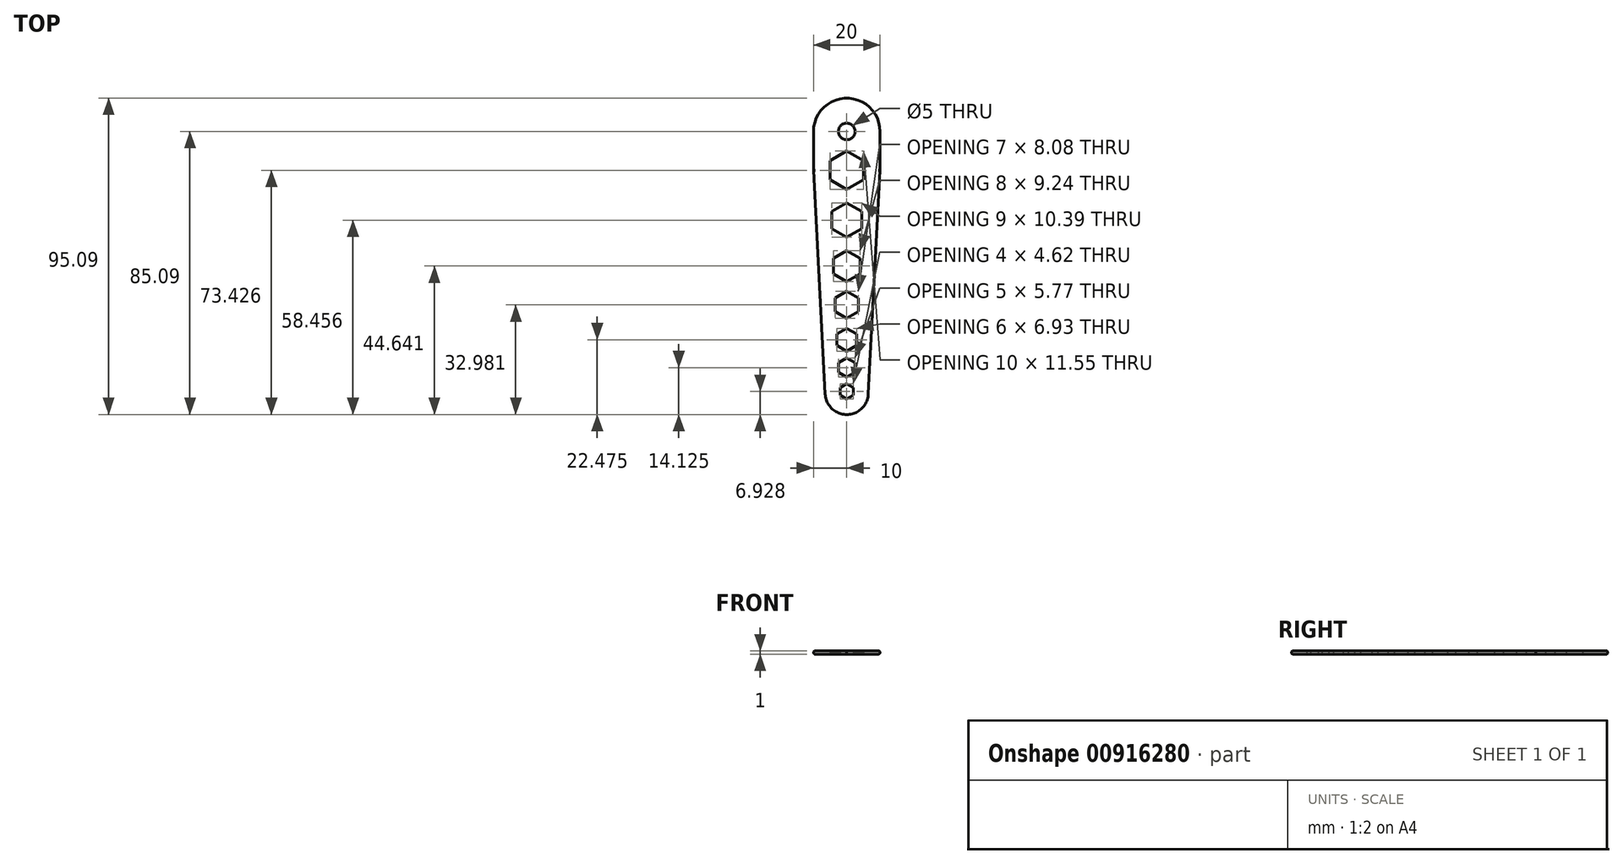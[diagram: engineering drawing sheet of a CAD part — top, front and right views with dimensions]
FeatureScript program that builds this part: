
annotation { "Feature Type Name" : "Feature", "Feature Type Description" : "" }
export const myFeature = defineFeature(function(context is Context, id is Id, definition is map)
    precondition{}
    {
        {
            var Q0;
            Q0=qCreatedBy(makeId("Top.planeOp"),FACE);
            var sketch = newSketch(context, id + "F0", { "sketchPlane" : qUnion([Q0])});
            skLineSegment(sketch, "E0.bottom", {"start": v(-10, 45) * mm, "end": v(10, 45) * mm, "construction": true});
            skLineSegment(sketch, "E0.left", {"start": v(-10, 45) * mm, "end": v(-10, -45) * mm, "construction": true});
            skLineSegment(sketch, "E0.right", {"start": v(10, 45) * mm, "end": v(10, -45) * mm, "construction": true});
            skPoint(sketch, "E0.middle", {"position": v(0, 0) * mm});
            skLineSegment(sketch, "E1", {"start": v(10, 35) * mm, "end": v(10, 23.34) * mm});
            skLineSegment(sketch, "E2", {"start": v(10, 23.34) * mm, "end": v(6.16, -50.09) * mm});
            skLineSegment(sketch, "E3", {"start": v(6.16, -50.09) * mm, "end": v(0, -50.09) * mm});
            skLineSegment(sketch, "E4", {"start": v(0, 45) * mm, "end": v(0, 45) * mm});
            skLineSegment(sketch, "E5.MirrorCS", {"start": v(-10, 23.34) * mm, "end": v(-6.16, -50.09) * mm});
            skLineSegment(sketch, "E6", {"start": v(-10, 23.34) * mm, "end": v(-10, 35) * mm});
            skLineSegment(sketch, "E7", {"start": v(-6.16, -50.09) * mm, "end": v(0, -50.09) * mm});
            skCircle(sketch, "E8", {"center": v(0, 35) * mm, "radius": 2.5 * mm});
            skPoint(sketch, "E9.visualSharp", {"position": v(-10, 45) * mm});
            skArc(sketch, "E9.filletArc", {"start": v(0, 45) * mm, "mid": v(-7.07, 42.07) * mm, "end": v(-10, 35) * mm});
            skPoint(sketch, "E10.visualSharp", {"position": v(10, 45) * mm});
            skArc(sketch, "E10.filletArc", {"start": v(10, 35) * mm, "mid": v(7.07, 42.07) * mm, "end": v(0, 45) * mm});
            skCircle(sketch, "E11.cCircle", {"center": v(0, 23.34) * mm, "radius": 5 * mm, "construction": true});
            skLineSegment(sketch, "E11.0", {"start": v(5, 26.22) * mm, "end": v(5, 20.45) * mm});
            skLineSegment(sketch, "E11.1", {"start": v(5, 20.45) * mm, "end": v(0, 17.56) * mm});
            skLineSegment(sketch, "E11.2", {"start": v(0, 17.56) * mm, "end": v(-5, 20.45) * mm});
            skLineSegment(sketch, "E11.3", {"start": v(-5, 20.45) * mm, "end": v(-5, 26.22) * mm});
            skLineSegment(sketch, "E11.4", {"start": v(-5, 26.22) * mm, "end": v(0, 29.1) * mm});
            skLineSegment(sketch, "E11.5", {"start": v(0, 29.1) * mm, "end": v(5, 26.22) * mm});
            skPoint(sketch, "E11.0.midPoint", {"position": v(5, 23.34) * mm});
            skCircle(sketch, "E12.cCircle", {"center": v(0, -27.61) * mm, "radius": 3 * mm, "construction": true});
            skLineSegment(sketch, "E12.0", {"start": v(3, -25.88) * mm, "end": v(3, -29.35) * mm});
            skLineSegment(sketch, "E12.1", {"start": v(3, -29.35) * mm, "end": v(0, -31.08) * mm});
            skLineSegment(sketch, "E12.2", {"start": v(0, -31.08) * mm, "end": v(-3, -29.35) * mm});
            skLineSegment(sketch, "E12.3", {"start": v(-3, -29.35) * mm, "end": v(-3, -25.88) * mm});
            skLineSegment(sketch, "E12.4", {"start": v(-3, -25.88) * mm, "end": v(0, -24.15) * mm});
            skLineSegment(sketch, "E12.5", {"start": v(0, -24.15) * mm, "end": v(3, -25.88) * mm});
            skPoint(sketch, "E12.0.midPoint", {"position": v(3, -27.61) * mm});
            skCircle(sketch, "E13.cCircle", {"center": v(0, -35.97) * mm, "radius": 2.5 * mm, "construction": true});
            skLineSegment(sketch, "E13.0", {"start": v(2.5, -34.52) * mm, "end": v(2.5, -37.4) * mm});
            skLineSegment(sketch, "E13.1", {"start": v(2.5, -37.4) * mm, "end": v(0, -38.85) * mm});
            skLineSegment(sketch, "E13.2", {"start": v(0, -38.85) * mm, "end": v(-2.5, -37.4) * mm});
            skLineSegment(sketch, "E13.3", {"start": v(-2.5, -37.4) * mm, "end": v(-2.5, -34.52) * mm});
            skLineSegment(sketch, "E13.4", {"start": v(-2.5, -34.52) * mm, "end": v(0, -33.08) * mm});
            skLineSegment(sketch, "E13.5", {"start": v(0, -33.08) * mm, "end": v(2.5, -34.52) * mm});
            skPoint(sketch, "E13.0.midPoint", {"position": v(2.5, -35.97) * mm});
            skCircle(sketch, "E14.cCircle", {"center": v(0, -43.16) * mm, "radius": 2 * mm, "construction": true});
            skLineSegment(sketch, "E14.0", {"start": v(2, -42) * mm, "end": v(2, -44.32) * mm});
            skLineSegment(sketch, "E14.1", {"start": v(2, -44.32) * mm, "end": v(0, -45.47) * mm});
            skLineSegment(sketch, "E14.2", {"start": v(0, -45.47) * mm, "end": v(-2, -44.32) * mm});
            skLineSegment(sketch, "E14.3", {"start": v(-2, -44.32) * mm, "end": v(-2, -42) * mm});
            skLineSegment(sketch, "E14.4", {"start": v(-2, -42) * mm, "end": v(0, -40.85) * mm});
            skLineSegment(sketch, "E14.5", {"start": v(0, -40.85) * mm, "end": v(2, -42) * mm});
            skPoint(sketch, "E14.0.midPoint", {"position": v(2, -43.16) * mm});
            skCircle(sketch, "E15.cCircle", {"center": v(0, 8.37) * mm, "radius": 4.5 * mm, "construction": true});
            skLineSegment(sketch, "E15.0", {"start": v(4.5, 10.96) * mm, "end": v(4.5, 5.77) * mm});
            skLineSegment(sketch, "E15.1", {"start": v(4.5, 5.77) * mm, "end": v(0, 3.17) * mm});
            skLineSegment(sketch, "E15.2", {"start": v(0, 3.17) * mm, "end": v(-4.5, 5.77) * mm});
            skLineSegment(sketch, "E15.3", {"start": v(-4.5, 5.77) * mm, "end": v(-4.5, 10.96) * mm});
            skLineSegment(sketch, "E15.4", {"start": v(-4.5, 10.96) * mm, "end": v(0, 13.56) * mm});
            skLineSegment(sketch, "E15.5", {"start": v(0, 13.56) * mm, "end": v(4.5, 10.96) * mm});
            skPoint(sketch, "E15.0.midPoint", {"position": v(4.5, 8.37) * mm});
            skCircle(sketch, "E16.cCircle", {"center": v(0, -5.45) * mm, "radius": 4 * mm, "construction": true});
            skLineSegment(sketch, "E16.0", {"start": v(4, -3.14) * mm, "end": v(4, -7.76) * mm});
            skLineSegment(sketch, "E16.1", {"start": v(4, -7.76) * mm, "end": v(0, -10.07) * mm});
            skLineSegment(sketch, "E16.2", {"start": v(0, -10.07) * mm, "end": v(-4, -7.76) * mm});
            skLineSegment(sketch, "E16.3", {"start": v(-4, -7.76) * mm, "end": v(-4, -3.14) * mm});
            skLineSegment(sketch, "E16.4", {"start": v(-4, -3.14) * mm, "end": v(0, -0.83) * mm});
            skLineSegment(sketch, "E16.5", {"start": v(0, -0.83) * mm, "end": v(4, -3.14) * mm});
            skPoint(sketch, "E16.0.midPoint", {"position": v(4, -5.45) * mm});
            skCircle(sketch, "E17.cCircle", {"center": v(0, -17.1) * mm, "radius": 3.5 * mm, "construction": true});
            skLineSegment(sketch, "E17.0", {"start": v(3.5, -15.09) * mm, "end": v(3.5, -19.13) * mm});
            skLineSegment(sketch, "E17.1", {"start": v(3.5, -19.13) * mm, "end": v(0, -21.15) * mm});
            skLineSegment(sketch, "E17.2", {"start": v(0, -21.15) * mm, "end": v(-3.5, -19.13) * mm});
            skLineSegment(sketch, "E17.3", {"start": v(-3.5, -19.13) * mm, "end": v(-3.5, -15.09) * mm});
            skLineSegment(sketch, "E17.4", {"start": v(-3.5, -15.09) * mm, "end": v(0, -13.07) * mm});
            skLineSegment(sketch, "E17.5", {"start": v(0, -13.07) * mm, "end": v(3.5, -15.09) * mm});
            skPoint(sketch, "E17.0.midPoint", {"position": v(3.5, -17.1) * mm});
            skSolve(sketch);
        }
        {
            var Q0;
            Q0=makeQuery(id+"F0.imprint","IMPRINT",FACE,{"disambiguationData":[TD([[makeQuery(id+"F0.imprint","IMPRINT",EDGE,{"derivedFrom":sQuery(id+"F0.wireOp",EDGE,"660UfFcq-DxuX-vggt-8gqN-h0Q4Ah5XbNWX")}),-1.0]])]});
            var Q1;
            Q1=makeQuery(id+"F0.imprint","IMPRINT",FACE,{"disambiguationData":[TD([[makeQuery(id+"F0.imprint","IMPRINT",EDGE,{"derivedFrom":sQuery(id+"F0.wireOp",EDGE,"E1")}),-1.0]])]});
            extrude(context, id + "F1", {"entities" : qUnion([Q0, Q1]), "depth" : 1 * mm, "offsetDistance" : 25 * mm});
        }
        {
            var Q0;
            Q0=makeQuery(id+"F1.opExtrude","SWEPT_EDGE",EDGE,{"disambiguationData":[OSD([sQuery(id+"F0.wireOp",EDGE,"E2"),sQuery(id+"F0.wireOp",EDGE,"E3")])]});
            var Q1;
            Q1=makeQuery(id+"F1.opExtrude","SWEPT_EDGE",EDGE,{"disambiguationData":[OSD([sQuery(id+"F0.wireOp",EDGE,"E5.MirrorCS"),sQuery(id+"F0.wireOp",EDGE,"E7")])]});
            fillet(context, id + "F2", {"entities" : qUnion([Q0, Q1]), "radius" : 6.5 * mm, "tangentPropagation" : true, "allowEdgeOverflow" : false});
        }
        {
            var Q0;
            Q0=makeQuery(id+"F1.opExtrude","CAP_EDGE",EDGE,{"disambiguationData":[OSD([sQuery(id+"F0.wireOp",EDGE,"E2")])],"isStart":false});
            var Q1;
            {var subQ0=sQuery(id+"F0.wireOp",EDGE,"E3");var subQ1=sQuery(id+"F0.wireOp",EDGE,"E2");Q1=makeQuery(id+"F2.opFillet","BLEND_EDGE",EDGE,{"blendedFrom":[makeQuery(id+"F1.opExtrude","SWEPT_EDGE",EDGE,{"disambiguationData":[OSD([subQ1,subQ0])]}),makeQuery(id+"F1.opExtrude","CAP_FACE",FACE,{"disambiguationData":[OSD([sQuery(id+"F0.wireOp",EDGE,"E1"),subQ1,subQ0,sQuery(id+"F0.wireOp",EDGE,"E5.MirrorCS"),sQuery(id+"F0.wireOp",EDGE,"E6"),sQuery(id+"F0.wireOp",EDGE,"E7"),sQuery(id+"F0.wireOp",EDGE,"E8"),sQuery(id+"F0.wireOp",EDGE,"E9.filletArc"),sQuery(id+"F0.wireOp",EDGE,"E10.filletArc"),sQuery(id+"F0.wireOp",EDGE,"E11.0"),sQuery(id+"F0.wireOp",EDGE,"E11.1"),sQuery(id+"F0.wireOp",EDGE,"E11.2"),sQuery(id+"F0.wireOp",EDGE,"E11.3"),sQuery(id+"F0.wireOp",EDGE,"E11.4"),sQuery(id+"F0.wireOp",EDGE,"E11.5"),sQuery(id+"F0.wireOp",EDGE,"E12.0"),sQuery(id+"F0.wireOp",EDGE,"E12.1"),sQuery(id+"F0.wireOp",EDGE,"E12.2"),sQuery(id+"F0.wireOp",EDGE,"E12.3"),sQuery(id+"F0.wireOp",EDGE,"E12.4"),sQuery(id+"F0.wireOp",EDGE,"E12.5"),sQuery(id+"F0.wireOp",EDGE,"E13.0"),sQuery(id+"F0.wireOp",EDGE,"E13.1"),sQuery(id+"F0.wireOp",EDGE,"E13.2"),sQuery(id+"F0.wireOp",EDGE,"E13.3"),sQuery(id+"F0.wireOp",EDGE,"E13.4"),sQuery(id+"F0.wireOp",EDGE,"E13.5"),sQuery(id+"F0.wireOp",EDGE,"E14.0"),sQuery(id+"F0.wireOp",EDGE,"E14.1"),sQuery(id+"F0.wireOp",EDGE,"E14.2"),sQuery(id+"F0.wireOp",EDGE,"E14.3"),sQuery(id+"F0.wireOp",EDGE,"E14.4"),sQuery(id+"F0.wireOp",EDGE,"E14.5"),sQuery(id+"F0.wireOp",EDGE,"E15.0"),sQuery(id+"F0.wireOp",EDGE,"E15.1"),sQuery(id+"F0.wireOp",EDGE,"E15.2"),sQuery(id+"F0.wireOp",EDGE,"E15.3"),sQuery(id+"F0.wireOp",EDGE,"E15.4"),sQuery(id+"F0.wireOp",EDGE,"E15.5"),sQuery(id+"F0.wireOp",EDGE,"E16.0"),sQuery(id+"F0.wireOp",EDGE,"E16.1"),sQuery(id+"F0.wireOp",EDGE,"E16.2"),sQuery(id+"F0.wireOp",EDGE,"E16.3"),sQuery(id+"F0.wireOp",EDGE,"E16.4"),sQuery(id+"F0.wireOp",EDGE,"E16.5"),sQuery(id+"F0.wireOp",EDGE,"E17.0"),sQuery(id+"F0.wireOp",EDGE,"E17.1"),sQuery(id+"F0.wireOp",EDGE,"E17.2"),sQuery(id+"F0.wireOp",EDGE,"E17.3"),sQuery(id+"F0.wireOp",EDGE,"E17.4"),sQuery(id+"F0.wireOp",EDGE,"E17.5")])],"isStart":false})],"blendedInto":[makeQuery(id+"F1.opExtrude","CAP_FACE",FACE,{"disambiguationData":[OSD([sQuery(id+"F0.wireOp",EDGE,"E1"),subQ1,subQ0,sQuery(id+"F0.wireOp",EDGE,"E5.MirrorCS"),sQuery(id+"F0.wireOp",EDGE,"E6"),sQuery(id+"F0.wireOp",EDGE,"E7"),sQuery(id+"F0.wireOp",EDGE,"E8"),sQuery(id+"F0.wireOp",EDGE,"E9.filletArc"),sQuery(id+"F0.wireOp",EDGE,"E10.filletArc"),sQuery(id+"F0.wireOp",EDGE,"E11.0"),sQuery(id+"F0.wireOp",EDGE,"E11.1"),sQuery(id+"F0.wireOp",EDGE,"E11.2"),sQuery(id+"F0.wireOp",EDGE,"E11.3"),sQuery(id+"F0.wireOp",EDGE,"E11.4"),sQuery(id+"F0.wireOp",EDGE,"E11.5"),sQuery(id+"F0.wireOp",EDGE,"E12.0"),sQuery(id+"F0.wireOp",EDGE,"E12.1"),sQuery(id+"F0.wireOp",EDGE,"E12.2"),sQuery(id+"F0.wireOp",EDGE,"E12.3"),sQuery(id+"F0.wireOp",EDGE,"E12.4"),sQuery(id+"F0.wireOp",EDGE,"E12.5"),sQuery(id+"F0.wireOp",EDGE,"E13.0"),sQuery(id+"F0.wireOp",EDGE,"E13.1"),sQuery(id+"F0.wireOp",EDGE,"E13.2"),sQuery(id+"F0.wireOp",EDGE,"E13.3"),sQuery(id+"F0.wireOp",EDGE,"E13.4"),sQuery(id+"F0.wireOp",EDGE,"E13.5"),sQuery(id+"F0.wireOp",EDGE,"E14.0"),sQuery(id+"F0.wireOp",EDGE,"E14.1"),sQuery(id+"F0.wireOp",EDGE,"E14.2"),sQuery(id+"F0.wireOp",EDGE,"E14.3"),sQuery(id+"F0.wireOp",EDGE,"E14.4"),sQuery(id+"F0.wireOp",EDGE,"E14.5"),sQuery(id+"F0.wireOp",EDGE,"E15.0"),sQuery(id+"F0.wireOp",EDGE,"E15.1"),sQuery(id+"F0.wireOp",EDGE,"E15.2"),sQuery(id+"F0.wireOp",EDGE,"E15.3"),sQuery(id+"F0.wireOp",EDGE,"E15.4"),sQuery(id+"F0.wireOp",EDGE,"E15.5"),sQuery(id+"F0.wireOp",EDGE,"E16.0"),sQuery(id+"F0.wireOp",EDGE,"E16.1"),sQuery(id+"F0.wireOp",EDGE,"E16.2"),sQuery(id+"F0.wireOp",EDGE,"E16.3"),sQuery(id+"F0.wireOp",EDGE,"E16.4"),sQuery(id+"F0.wireOp",EDGE,"E16.5"),sQuery(id+"F0.wireOp",EDGE,"E17.0"),sQuery(id+"F0.wireOp",EDGE,"E17.1"),sQuery(id+"F0.wireOp",EDGE,"E17.2"),sQuery(id+"F0.wireOp",EDGE,"E17.3"),sQuery(id+"F0.wireOp",EDGE,"E17.4"),sQuery(id+"F0.wireOp",EDGE,"E17.5")])],"isStart":false})]});}
            var Q2;
            {var subQ0=sQuery(id+"F0.wireOp",EDGE,"E7");var subQ1=sQuery(id+"F0.wireOp",EDGE,"E5.MirrorCS");Q2=makeQuery(id+"F2.opFillet","BLEND_EDGE",EDGE,{"blendedFrom":[makeQuery(id+"F1.opExtrude","SWEPT_EDGE",EDGE,{"disambiguationData":[OSD([subQ1,subQ0])]}),makeQuery(id+"F1.opExtrude","CAP_FACE",FACE,{"disambiguationData":[OSD([sQuery(id+"F0.wireOp",EDGE,"E1"),sQuery(id+"F0.wireOp",EDGE,"E2"),sQuery(id+"F0.wireOp",EDGE,"E3"),subQ1,sQuery(id+"F0.wireOp",EDGE,"E6"),subQ0,sQuery(id+"F0.wireOp",EDGE,"E8"),sQuery(id+"F0.wireOp",EDGE,"E9.filletArc"),sQuery(id+"F0.wireOp",EDGE,"E10.filletArc"),sQuery(id+"F0.wireOp",EDGE,"E11.0"),sQuery(id+"F0.wireOp",EDGE,"E11.1"),sQuery(id+"F0.wireOp",EDGE,"E11.2"),sQuery(id+"F0.wireOp",EDGE,"E11.3"),sQuery(id+"F0.wireOp",EDGE,"E11.4"),sQuery(id+"F0.wireOp",EDGE,"E11.5"),sQuery(id+"F0.wireOp",EDGE,"E12.0"),sQuery(id+"F0.wireOp",EDGE,"E12.1"),sQuery(id+"F0.wireOp",EDGE,"E12.2"),sQuery(id+"F0.wireOp",EDGE,"E12.3"),sQuery(id+"F0.wireOp",EDGE,"E12.4"),sQuery(id+"F0.wireOp",EDGE,"E12.5"),sQuery(id+"F0.wireOp",EDGE,"E13.0"),sQuery(id+"F0.wireOp",EDGE,"E13.1"),sQuery(id+"F0.wireOp",EDGE,"E13.2"),sQuery(id+"F0.wireOp",EDGE,"E13.3"),sQuery(id+"F0.wireOp",EDGE,"E13.4"),sQuery(id+"F0.wireOp",EDGE,"E13.5"),sQuery(id+"F0.wireOp",EDGE,"E14.0"),sQuery(id+"F0.wireOp",EDGE,"E14.1"),sQuery(id+"F0.wireOp",EDGE,"E14.2"),sQuery(id+"F0.wireOp",EDGE,"E14.3"),sQuery(id+"F0.wireOp",EDGE,"E14.4"),sQuery(id+"F0.wireOp",EDGE,"E14.5"),sQuery(id+"F0.wireOp",EDGE,"E15.0"),sQuery(id+"F0.wireOp",EDGE,"E15.1"),sQuery(id+"F0.wireOp",EDGE,"E15.2"),sQuery(id+"F0.wireOp",EDGE,"E15.3"),sQuery(id+"F0.wireOp",EDGE,"E15.4"),sQuery(id+"F0.wireOp",EDGE,"E15.5"),sQuery(id+"F0.wireOp",EDGE,"E16.0"),sQuery(id+"F0.wireOp",EDGE,"E16.1"),sQuery(id+"F0.wireOp",EDGE,"E16.2"),sQuery(id+"F0.wireOp",EDGE,"E16.3"),sQuery(id+"F0.wireOp",EDGE,"E16.4"),sQuery(id+"F0.wireOp",EDGE,"E16.5"),sQuery(id+"F0.wireOp",EDGE,"E17.0"),sQuery(id+"F0.wireOp",EDGE,"E17.1"),sQuery(id+"F0.wireOp",EDGE,"E17.2"),sQuery(id+"F0.wireOp",EDGE,"E17.3"),sQuery(id+"F0.wireOp",EDGE,"E17.4"),sQuery(id+"F0.wireOp",EDGE,"E17.5")])],"isStart":false})],"blendedInto":[makeQuery(id+"F1.opExtrude","CAP_FACE",FACE,{"disambiguationData":[OSD([sQuery(id+"F0.wireOp",EDGE,"E1"),sQuery(id+"F0.wireOp",EDGE,"E2"),sQuery(id+"F0.wireOp",EDGE,"E3"),subQ1,sQuery(id+"F0.wireOp",EDGE,"E6"),subQ0,sQuery(id+"F0.wireOp",EDGE,"E8"),sQuery(id+"F0.wireOp",EDGE,"E9.filletArc"),sQuery(id+"F0.wireOp",EDGE,"E10.filletArc"),sQuery(id+"F0.wireOp",EDGE,"E11.0"),sQuery(id+"F0.wireOp",EDGE,"E11.1"),sQuery(id+"F0.wireOp",EDGE,"E11.2"),sQuery(id+"F0.wireOp",EDGE,"E11.3"),sQuery(id+"F0.wireOp",EDGE,"E11.4"),sQuery(id+"F0.wireOp",EDGE,"E11.5"),sQuery(id+"F0.wireOp",EDGE,"E12.0"),sQuery(id+"F0.wireOp",EDGE,"E12.1"),sQuery(id+"F0.wireOp",EDGE,"E12.2"),sQuery(id+"F0.wireOp",EDGE,"E12.3"),sQuery(id+"F0.wireOp",EDGE,"E12.4"),sQuery(id+"F0.wireOp",EDGE,"E12.5"),sQuery(id+"F0.wireOp",EDGE,"E13.0"),sQuery(id+"F0.wireOp",EDGE,"E13.1"),sQuery(id+"F0.wireOp",EDGE,"E13.2"),sQuery(id+"F0.wireOp",EDGE,"E13.3"),sQuery(id+"F0.wireOp",EDGE,"E13.4"),sQuery(id+"F0.wireOp",EDGE,"E13.5"),sQuery(id+"F0.wireOp",EDGE,"E14.0"),sQuery(id+"F0.wireOp",EDGE,"E14.1"),sQuery(id+"F0.wireOp",EDGE,"E14.2"),sQuery(id+"F0.wireOp",EDGE,"E14.3"),sQuery(id+"F0.wireOp",EDGE,"E14.4"),sQuery(id+"F0.wireOp",EDGE,"E14.5"),sQuery(id+"F0.wireOp",EDGE,"E15.0"),sQuery(id+"F0.wireOp",EDGE,"E15.1"),sQuery(id+"F0.wireOp",EDGE,"E15.2"),sQuery(id+"F0.wireOp",EDGE,"E15.3"),sQuery(id+"F0.wireOp",EDGE,"E15.4"),sQuery(id+"F0.wireOp",EDGE,"E15.5"),sQuery(id+"F0.wireOp",EDGE,"E16.0"),sQuery(id+"F0.wireOp",EDGE,"E16.1"),sQuery(id+"F0.wireOp",EDGE,"E16.2"),sQuery(id+"F0.wireOp",EDGE,"E16.3"),sQuery(id+"F0.wireOp",EDGE,"E16.4"),sQuery(id+"F0.wireOp",EDGE,"E16.5"),sQuery(id+"F0.wireOp",EDGE,"E17.0"),sQuery(id+"F0.wireOp",EDGE,"E17.1"),sQuery(id+"F0.wireOp",EDGE,"E17.2"),sQuery(id+"F0.wireOp",EDGE,"E17.3"),sQuery(id+"F0.wireOp",EDGE,"E17.4"),sQuery(id+"F0.wireOp",EDGE,"E17.5")])],"isStart":false})]});}
            var Q3;
            Q3=makeQuery(id+"F1.opExtrude","CAP_EDGE",EDGE,{"disambiguationData":[OSD([sQuery(id+"F0.wireOp",EDGE,"E5.MirrorCS")])],"isStart":false});
            var Q4;
            Q4=makeQuery(id+"F1.opExtrude","CAP_EDGE",EDGE,{"disambiguationData":[OSD([sQuery(id+"F0.wireOp",EDGE,"E1")])],"isStart":false});
            var Q5;
            Q5=makeQuery(id+"F1.opExtrude","CAP_EDGE",EDGE,{"disambiguationData":[OSD([sQuery(id+"F0.wireOp",EDGE,"E9.filletArc"),sQuery(id+"F0.wireOp",EDGE,"E10.filletArc")])],"isStart":false});
            var Q6;
            Q6=makeQuery(id+"F1.opExtrude","CAP_EDGE",EDGE,{"disambiguationData":[OSD([sQuery(id+"F0.wireOp",EDGE,"E6")])],"isStart":false});
            var Q7;
            {var subQ0=sQuery(id+"F0.wireOp",EDGE,"E3");var subQ1=sQuery(id+"F0.wireOp",EDGE,"E2");Q7=makeQuery(id+"F2.opFillet","BLEND_EDGE",EDGE,{"blendedFrom":[makeQuery(id+"F1.opExtrude","SWEPT_EDGE",EDGE,{"disambiguationData":[OSD([subQ1,subQ0])]}),makeQuery(id+"F1.opExtrude","CAP_FACE",FACE,{"disambiguationData":[OSD([sQuery(id+"F0.wireOp",EDGE,"E1"),subQ1,subQ0,sQuery(id+"F0.wireOp",EDGE,"E5.MirrorCS"),sQuery(id+"F0.wireOp",EDGE,"E6"),sQuery(id+"F0.wireOp",EDGE,"E7"),sQuery(id+"F0.wireOp",EDGE,"E8"),sQuery(id+"F0.wireOp",EDGE,"E9.filletArc"),sQuery(id+"F0.wireOp",EDGE,"E10.filletArc"),sQuery(id+"F0.wireOp",EDGE,"E11.0"),sQuery(id+"F0.wireOp",EDGE,"E11.1"),sQuery(id+"F0.wireOp",EDGE,"E11.2"),sQuery(id+"F0.wireOp",EDGE,"E11.3"),sQuery(id+"F0.wireOp",EDGE,"E11.4"),sQuery(id+"F0.wireOp",EDGE,"E11.5"),sQuery(id+"F0.wireOp",EDGE,"E12.0"),sQuery(id+"F0.wireOp",EDGE,"E12.1"),sQuery(id+"F0.wireOp",EDGE,"E12.2"),sQuery(id+"F0.wireOp",EDGE,"E12.3"),sQuery(id+"F0.wireOp",EDGE,"E12.4"),sQuery(id+"F0.wireOp",EDGE,"E12.5"),sQuery(id+"F0.wireOp",EDGE,"E13.0"),sQuery(id+"F0.wireOp",EDGE,"E13.1"),sQuery(id+"F0.wireOp",EDGE,"E13.2"),sQuery(id+"F0.wireOp",EDGE,"E13.3"),sQuery(id+"F0.wireOp",EDGE,"E13.4"),sQuery(id+"F0.wireOp",EDGE,"E13.5"),sQuery(id+"F0.wireOp",EDGE,"E14.0"),sQuery(id+"F0.wireOp",EDGE,"E14.1"),sQuery(id+"F0.wireOp",EDGE,"E14.2"),sQuery(id+"F0.wireOp",EDGE,"E14.3"),sQuery(id+"F0.wireOp",EDGE,"E14.4"),sQuery(id+"F0.wireOp",EDGE,"E14.5"),sQuery(id+"F0.wireOp",EDGE,"E15.0"),sQuery(id+"F0.wireOp",EDGE,"E15.1"),sQuery(id+"F0.wireOp",EDGE,"E15.2"),sQuery(id+"F0.wireOp",EDGE,"E15.3"),sQuery(id+"F0.wireOp",EDGE,"E15.4"),sQuery(id+"F0.wireOp",EDGE,"E15.5"),sQuery(id+"F0.wireOp",EDGE,"E16.0"),sQuery(id+"F0.wireOp",EDGE,"E16.1"),sQuery(id+"F0.wireOp",EDGE,"E16.2"),sQuery(id+"F0.wireOp",EDGE,"E16.3"),sQuery(id+"F0.wireOp",EDGE,"E16.4"),sQuery(id+"F0.wireOp",EDGE,"E16.5"),sQuery(id+"F0.wireOp",EDGE,"E17.0"),sQuery(id+"F0.wireOp",EDGE,"E17.1"),sQuery(id+"F0.wireOp",EDGE,"E17.2"),sQuery(id+"F0.wireOp",EDGE,"E17.3"),sQuery(id+"F0.wireOp",EDGE,"E17.4"),sQuery(id+"F0.wireOp",EDGE,"E17.5")])],"isStart":true})],"blendedInto":[makeQuery(id+"F1.opExtrude","CAP_FACE",FACE,{"disambiguationData":[OSD([sQuery(id+"F0.wireOp",EDGE,"E1"),subQ1,subQ0,sQuery(id+"F0.wireOp",EDGE,"E5.MirrorCS"),sQuery(id+"F0.wireOp",EDGE,"E6"),sQuery(id+"F0.wireOp",EDGE,"E7"),sQuery(id+"F0.wireOp",EDGE,"E8"),sQuery(id+"F0.wireOp",EDGE,"E9.filletArc"),sQuery(id+"F0.wireOp",EDGE,"E10.filletArc"),sQuery(id+"F0.wireOp",EDGE,"E11.0"),sQuery(id+"F0.wireOp",EDGE,"E11.1"),sQuery(id+"F0.wireOp",EDGE,"E11.2"),sQuery(id+"F0.wireOp",EDGE,"E11.3"),sQuery(id+"F0.wireOp",EDGE,"E11.4"),sQuery(id+"F0.wireOp",EDGE,"E11.5"),sQuery(id+"F0.wireOp",EDGE,"E12.0"),sQuery(id+"F0.wireOp",EDGE,"E12.1"),sQuery(id+"F0.wireOp",EDGE,"E12.2"),sQuery(id+"F0.wireOp",EDGE,"E12.3"),sQuery(id+"F0.wireOp",EDGE,"E12.4"),sQuery(id+"F0.wireOp",EDGE,"E12.5"),sQuery(id+"F0.wireOp",EDGE,"E13.0"),sQuery(id+"F0.wireOp",EDGE,"E13.1"),sQuery(id+"F0.wireOp",EDGE,"E13.2"),sQuery(id+"F0.wireOp",EDGE,"E13.3"),sQuery(id+"F0.wireOp",EDGE,"E13.4"),sQuery(id+"F0.wireOp",EDGE,"E13.5"),sQuery(id+"F0.wireOp",EDGE,"E14.0"),sQuery(id+"F0.wireOp",EDGE,"E14.1"),sQuery(id+"F0.wireOp",EDGE,"E14.2"),sQuery(id+"F0.wireOp",EDGE,"E14.3"),sQuery(id+"F0.wireOp",EDGE,"E14.4"),sQuery(id+"F0.wireOp",EDGE,"E14.5"),sQuery(id+"F0.wireOp",EDGE,"E15.0"),sQuery(id+"F0.wireOp",EDGE,"E15.1"),sQuery(id+"F0.wireOp",EDGE,"E15.2"),sQuery(id+"F0.wireOp",EDGE,"E15.3"),sQuery(id+"F0.wireOp",EDGE,"E15.4"),sQuery(id+"F0.wireOp",EDGE,"E15.5"),sQuery(id+"F0.wireOp",EDGE,"E16.0"),sQuery(id+"F0.wireOp",EDGE,"E16.1"),sQuery(id+"F0.wireOp",EDGE,"E16.2"),sQuery(id+"F0.wireOp",EDGE,"E16.3"),sQuery(id+"F0.wireOp",EDGE,"E16.4"),sQuery(id+"F0.wireOp",EDGE,"E16.5"),sQuery(id+"F0.wireOp",EDGE,"E17.0"),sQuery(id+"F0.wireOp",EDGE,"E17.1"),sQuery(id+"F0.wireOp",EDGE,"E17.2"),sQuery(id+"F0.wireOp",EDGE,"E17.3"),sQuery(id+"F0.wireOp",EDGE,"E17.4"),sQuery(id+"F0.wireOp",EDGE,"E17.5")])],"isStart":true})]});}
            var Q8;
            {var subQ0=sQuery(id+"F0.wireOp",EDGE,"E7");var subQ1=sQuery(id+"F0.wireOp",EDGE,"E5.MirrorCS");Q8=makeQuery(id+"F2.opFillet","BLEND_EDGE",EDGE,{"blendedFrom":[makeQuery(id+"F1.opExtrude","SWEPT_EDGE",EDGE,{"disambiguationData":[OSD([subQ1,subQ0])]}),makeQuery(id+"F1.opExtrude","CAP_FACE",FACE,{"disambiguationData":[OSD([sQuery(id+"F0.wireOp",EDGE,"E1"),sQuery(id+"F0.wireOp",EDGE,"E2"),sQuery(id+"F0.wireOp",EDGE,"E3"),subQ1,sQuery(id+"F0.wireOp",EDGE,"E6"),subQ0,sQuery(id+"F0.wireOp",EDGE,"E8"),sQuery(id+"F0.wireOp",EDGE,"E9.filletArc"),sQuery(id+"F0.wireOp",EDGE,"E10.filletArc"),sQuery(id+"F0.wireOp",EDGE,"E11.0"),sQuery(id+"F0.wireOp",EDGE,"E11.1"),sQuery(id+"F0.wireOp",EDGE,"E11.2"),sQuery(id+"F0.wireOp",EDGE,"E11.3"),sQuery(id+"F0.wireOp",EDGE,"E11.4"),sQuery(id+"F0.wireOp",EDGE,"E11.5"),sQuery(id+"F0.wireOp",EDGE,"E12.0"),sQuery(id+"F0.wireOp",EDGE,"E12.1"),sQuery(id+"F0.wireOp",EDGE,"E12.2"),sQuery(id+"F0.wireOp",EDGE,"E12.3"),sQuery(id+"F0.wireOp",EDGE,"E12.4"),sQuery(id+"F0.wireOp",EDGE,"E12.5"),sQuery(id+"F0.wireOp",EDGE,"E13.0"),sQuery(id+"F0.wireOp",EDGE,"E13.1"),sQuery(id+"F0.wireOp",EDGE,"E13.2"),sQuery(id+"F0.wireOp",EDGE,"E13.3"),sQuery(id+"F0.wireOp",EDGE,"E13.4"),sQuery(id+"F0.wireOp",EDGE,"E13.5"),sQuery(id+"F0.wireOp",EDGE,"E14.0"),sQuery(id+"F0.wireOp",EDGE,"E14.1"),sQuery(id+"F0.wireOp",EDGE,"E14.2"),sQuery(id+"F0.wireOp",EDGE,"E14.3"),sQuery(id+"F0.wireOp",EDGE,"E14.4"),sQuery(id+"F0.wireOp",EDGE,"E14.5"),sQuery(id+"F0.wireOp",EDGE,"E15.0"),sQuery(id+"F0.wireOp",EDGE,"E15.1"),sQuery(id+"F0.wireOp",EDGE,"E15.2"),sQuery(id+"F0.wireOp",EDGE,"E15.3"),sQuery(id+"F0.wireOp",EDGE,"E15.4"),sQuery(id+"F0.wireOp",EDGE,"E15.5"),sQuery(id+"F0.wireOp",EDGE,"E16.0"),sQuery(id+"F0.wireOp",EDGE,"E16.1"),sQuery(id+"F0.wireOp",EDGE,"E16.2"),sQuery(id+"F0.wireOp",EDGE,"E16.3"),sQuery(id+"F0.wireOp",EDGE,"E16.4"),sQuery(id+"F0.wireOp",EDGE,"E16.5"),sQuery(id+"F0.wireOp",EDGE,"E17.0"),sQuery(id+"F0.wireOp",EDGE,"E17.1"),sQuery(id+"F0.wireOp",EDGE,"E17.2"),sQuery(id+"F0.wireOp",EDGE,"E17.3"),sQuery(id+"F0.wireOp",EDGE,"E17.4"),sQuery(id+"F0.wireOp",EDGE,"E17.5")])],"isStart":true})],"blendedInto":[makeQuery(id+"F1.opExtrude","CAP_FACE",FACE,{"disambiguationData":[OSD([sQuery(id+"F0.wireOp",EDGE,"E1"),sQuery(id+"F0.wireOp",EDGE,"E2"),sQuery(id+"F0.wireOp",EDGE,"E3"),subQ1,sQuery(id+"F0.wireOp",EDGE,"E6"),subQ0,sQuery(id+"F0.wireOp",EDGE,"E8"),sQuery(id+"F0.wireOp",EDGE,"E9.filletArc"),sQuery(id+"F0.wireOp",EDGE,"E10.filletArc"),sQuery(id+"F0.wireOp",EDGE,"E11.0"),sQuery(id+"F0.wireOp",EDGE,"E11.1"),sQuery(id+"F0.wireOp",EDGE,"E11.2"),sQuery(id+"F0.wireOp",EDGE,"E11.3"),sQuery(id+"F0.wireOp",EDGE,"E11.4"),sQuery(id+"F0.wireOp",EDGE,"E11.5"),sQuery(id+"F0.wireOp",EDGE,"E12.0"),sQuery(id+"F0.wireOp",EDGE,"E12.1"),sQuery(id+"F0.wireOp",EDGE,"E12.2"),sQuery(id+"F0.wireOp",EDGE,"E12.3"),sQuery(id+"F0.wireOp",EDGE,"E12.4"),sQuery(id+"F0.wireOp",EDGE,"E12.5"),sQuery(id+"F0.wireOp",EDGE,"E13.0"),sQuery(id+"F0.wireOp",EDGE,"E13.1"),sQuery(id+"F0.wireOp",EDGE,"E13.2"),sQuery(id+"F0.wireOp",EDGE,"E13.3"),sQuery(id+"F0.wireOp",EDGE,"E13.4"),sQuery(id+"F0.wireOp",EDGE,"E13.5"),sQuery(id+"F0.wireOp",EDGE,"E14.0"),sQuery(id+"F0.wireOp",EDGE,"E14.1"),sQuery(id+"F0.wireOp",EDGE,"E14.2"),sQuery(id+"F0.wireOp",EDGE,"E14.3"),sQuery(id+"F0.wireOp",EDGE,"E14.4"),sQuery(id+"F0.wireOp",EDGE,"E14.5"),sQuery(id+"F0.wireOp",EDGE,"E15.0"),sQuery(id+"F0.wireOp",EDGE,"E15.1"),sQuery(id+"F0.wireOp",EDGE,"E15.2"),sQuery(id+"F0.wireOp",EDGE,"E15.3"),sQuery(id+"F0.wireOp",EDGE,"E15.4"),sQuery(id+"F0.wireOp",EDGE,"E15.5"),sQuery(id+"F0.wireOp",EDGE,"E16.0"),sQuery(id+"F0.wireOp",EDGE,"E16.1"),sQuery(id+"F0.wireOp",EDGE,"E16.2"),sQuery(id+"F0.wireOp",EDGE,"E16.3"),sQuery(id+"F0.wireOp",EDGE,"E16.4"),sQuery(id+"F0.wireOp",EDGE,"E16.5"),sQuery(id+"F0.wireOp",EDGE,"E17.0"),sQuery(id+"F0.wireOp",EDGE,"E17.1"),sQuery(id+"F0.wireOp",EDGE,"E17.2"),sQuery(id+"F0.wireOp",EDGE,"E17.3"),sQuery(id+"F0.wireOp",EDGE,"E17.4"),sQuery(id+"F0.wireOp",EDGE,"E17.5")])],"isStart":true})]});}
            var Q9;
            Q9=makeQuery(id+"F1.opExtrude","CAP_EDGE",EDGE,{"disambiguationData":[OSD([sQuery(id+"F0.wireOp",EDGE,"E9.filletArc"),sQuery(id+"F0.wireOp",EDGE,"E10.filletArc")])],"isStart":true});
            fillet(context, id + "F3", {"entities" : qUnion([Q0, Q1, Q2, Q3, Q4, Q5, Q6, Q7, Q8, Q9]), "radius" : 0.5 * mm, "tangentPropagation" : true, "allowEdgeOverflow" : false});
        }
    });
